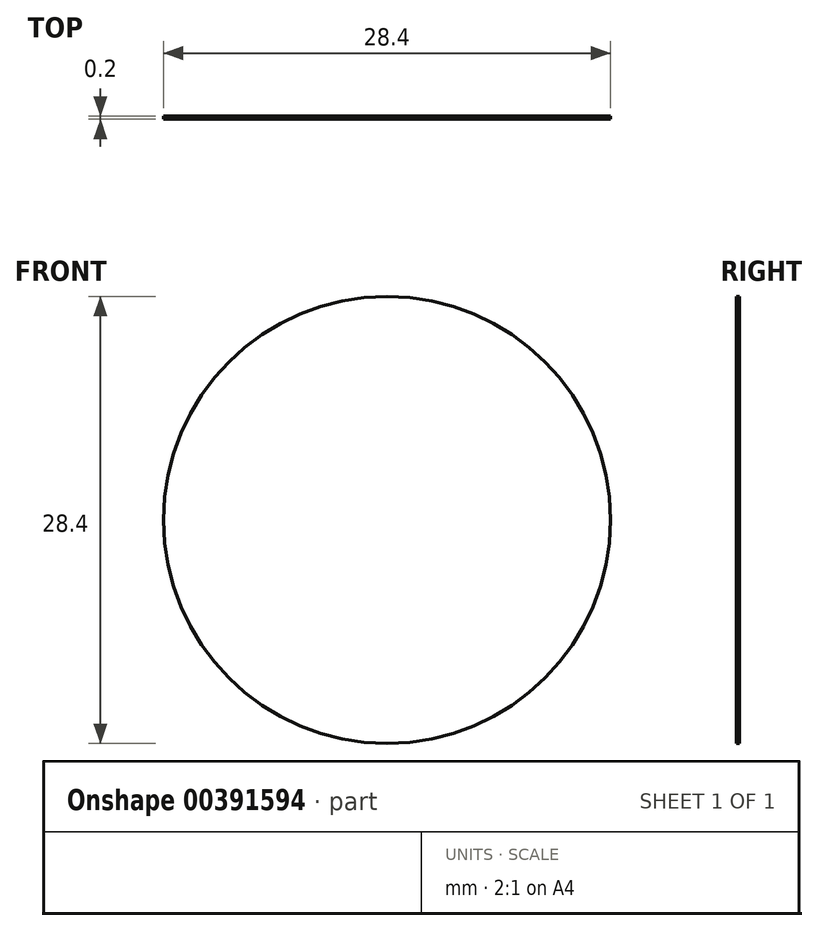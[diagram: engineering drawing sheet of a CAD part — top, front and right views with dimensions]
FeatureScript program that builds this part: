
annotation { "Feature Type Name" : "Feature", "Feature Type Description" : "" }
export const myFeature = defineFeature(function(context is Context, id is Id, definition is map)
    precondition{}
    {
        {
            var Q0;
            Q0=qCreatedBy(makeId("Front.planeOp"),FACE);
            var sketch = newSketch(context, id + "F0", { "sketchPlane" : qUnion([Q0])});
            skCircle(sketch, "E0", {"center": v(0, 0) * mm, "radius": 8 * mm, "construction": true});
            skCircle(sketch, "E1", {"center": v(0, 0) * mm, "radius": 10.5 * mm, "construction": true});
            skLineSegment(sketch, "E2", {"start": v(0, 8) * mm, "end": v(0.75, 8) * mm, "construction": true});
            skLineSegment(sketch, "E3", {"start": v(0.75, 8) * mm, "end": v(0.75, 13.5) * mm, "construction": true});
            skLineSegment(sketch, "E4", {"start": v(0.75, 13.5) * mm, "end": v(0, 13.5) * mm, "construction": true});
            skLineSegment(sketch, "E5", {"start": v(0, 13.5) * mm, "end": v(-0.75, 13.5) * mm, "construction": true});
            skLineSegment(sketch, "E6", {"start": v(-0.75, 13.5) * mm, "end": v(-0.75, 8) * mm, "construction": true});
            skLineSegment(sketch, "E7", {"start": v(-0.75, 8) * mm, "end": v(0, 8) * mm, "construction": true});
            skLineSegment(sketch, "E8.1.0", {"start": v(-3.35, 7.3) * mm, "end": v(-6.1, 12.07) * mm});
            skLineSegment(sketch, "E8.1.1", {"start": v(-7.4, 11.32) * mm, "end": v(-4.65, 6.55) * mm});
            skLineSegment(sketch, "E8.1.2", {"start": v(-4.65, 6.55) * mm, "end": v(-4, 6.93) * mm});
            skLineSegment(sketch, "E8.1.3", {"start": v(-4, 6.93) * mm, "end": v(-3.35, 7.3) * mm});
            skLineSegment(sketch, "E8.1.4", {"start": v(-6.1, 12.07) * mm, "end": v(-6.75, 11.7) * mm});
            skLineSegment(sketch, "E8.1.5", {"start": v(-6.75, 11.7) * mm, "end": v(-7.4, 11.32) * mm});
            skLineSegment(sketch, "E8.2.0", {"start": v(-6.55, 4.65) * mm, "end": v(-11.32, 7.4) * mm});
            skLineSegment(sketch, "E8.2.1", {"start": v(-12.07, 6.1) * mm, "end": v(-7.3, 3.35) * mm});
            skLineSegment(sketch, "E8.2.2", {"start": v(-7.3, 3.35) * mm, "end": v(-6.93, 4) * mm});
            skLineSegment(sketch, "E8.2.3", {"start": v(-6.93, 4) * mm, "end": v(-6.55, 4.65) * mm});
            skLineSegment(sketch, "E8.2.4", {"start": v(-11.32, 7.4) * mm, "end": v(-11.7, 6.75) * mm});
            skLineSegment(sketch, "E8.2.5", {"start": v(-11.7, 6.75) * mm, "end": v(-12.07, 6.1) * mm});
            skLineSegment(sketch, "E8.3.0", {"start": v(-8, 0.75) * mm, "end": v(-13.5, 0.75) * mm, "construction": true});
            skLineSegment(sketch, "E8.3.1", {"start": v(-13.5, -0.75) * mm, "end": v(-8, -0.75) * mm, "construction": true});
            skLineSegment(sketch, "E8.3.2", {"start": v(-8, -0.75) * mm, "end": v(-8, 0) * mm, "construction": true});
            skLineSegment(sketch, "E8.3.3", {"start": v(-8, 0) * mm, "end": v(-8, 0.75) * mm, "construction": true});
            skLineSegment(sketch, "E8.3.4", {"start": v(-13.5, 0.75) * mm, "end": v(-13.5, 0) * mm, "construction": true});
            skLineSegment(sketch, "E8.3.5", {"start": v(-13.5, 0) * mm, "end": v(-13.5, -0.75) * mm, "construction": true});
            skLineSegment(sketch, "E8.4.0", {"start": v(-7.3, -3.35) * mm, "end": v(-12.07, -6.1) * mm});
            skLineSegment(sketch, "E8.4.1", {"start": v(-11.32, -7.4) * mm, "end": v(-6.55, -4.65) * mm});
            skLineSegment(sketch, "E8.4.2", {"start": v(-6.55, -4.65) * mm, "end": v(-6.93, -4) * mm});
            skLineSegment(sketch, "E8.4.3", {"start": v(-6.93, -4) * mm, "end": v(-7.3, -3.35) * mm});
            skLineSegment(sketch, "E8.4.4", {"start": v(-12.07, -6.1) * mm, "end": v(-11.7, -6.75) * mm});
            skLineSegment(sketch, "E8.4.5", {"start": v(-11.7, -6.75) * mm, "end": v(-11.32, -7.4) * mm});
            skLineSegment(sketch, "E8.5.0", {"start": v(-4.65, -6.55) * mm, "end": v(-7.4, -11.32) * mm});
            skLineSegment(sketch, "E8.5.1", {"start": v(-6.1, -12.07) * mm, "end": v(-3.35, -7.3) * mm});
            skLineSegment(sketch, "E8.5.2", {"start": v(-3.35, -7.3) * mm, "end": v(-4, -6.93) * mm});
            skLineSegment(sketch, "E8.5.3", {"start": v(-4, -6.93) * mm, "end": v(-4.65, -6.55) * mm});
            skLineSegment(sketch, "E8.5.4", {"start": v(-7.4, -11.32) * mm, "end": v(-6.75, -11.7) * mm});
            skLineSegment(sketch, "E8.5.5", {"start": v(-6.75, -11.7) * mm, "end": v(-6.1, -12.07) * mm});
            skLineSegment(sketch, "E8.6.0", {"start": v(-0.75, -8) * mm, "end": v(-0.75, -13.5) * mm, "construction": true});
            skLineSegment(sketch, "E8.6.1", {"start": v(0.75, -13.5) * mm, "end": v(0.75, -8) * mm, "construction": true});
            skLineSegment(sketch, "E8.6.2", {"start": v(0.75, -8) * mm, "end": v(0, -8) * mm, "construction": true});
            skLineSegment(sketch, "E8.6.3", {"start": v(0, -8) * mm, "end": v(-0.75, -8) * mm, "construction": true});
            skLineSegment(sketch, "E8.6.4", {"start": v(-0.75, -13.5) * mm, "end": v(0, -13.5) * mm, "construction": true});
            skLineSegment(sketch, "E8.6.5", {"start": v(0, -13.5) * mm, "end": v(0.75, -13.5) * mm, "construction": true});
            skLineSegment(sketch, "E8.7.0", {"start": v(3.35, -7.3) * mm, "end": v(6.1, -12.07) * mm});
            skLineSegment(sketch, "E8.7.1", {"start": v(7.4, -11.32) * mm, "end": v(4.65, -6.55) * mm});
            skLineSegment(sketch, "E8.7.2", {"start": v(4.65, -6.55) * mm, "end": v(4, -6.93) * mm});
            skLineSegment(sketch, "E8.7.3", {"start": v(4, -6.93) * mm, "end": v(3.35, -7.3) * mm});
            skLineSegment(sketch, "E8.7.4", {"start": v(6.1, -12.07) * mm, "end": v(6.75, -11.7) * mm});
            skLineSegment(sketch, "E8.7.5", {"start": v(6.75, -11.7) * mm, "end": v(7.4, -11.32) * mm});
            skLineSegment(sketch, "E8.8.0", {"start": v(6.55, -4.65) * mm, "end": v(11.32, -7.4) * mm});
            skLineSegment(sketch, "E8.8.1", {"start": v(12.07, -6.1) * mm, "end": v(7.3, -3.35) * mm});
            skLineSegment(sketch, "E8.8.2", {"start": v(7.3, -3.35) * mm, "end": v(6.93, -4) * mm});
            skLineSegment(sketch, "E8.8.3", {"start": v(6.93, -4) * mm, "end": v(6.55, -4.65) * mm});
            skLineSegment(sketch, "E8.8.4", {"start": v(11.32, -7.4) * mm, "end": v(11.7, -6.75) * mm});
            skLineSegment(sketch, "E8.8.5", {"start": v(11.7, -6.75) * mm, "end": v(12.07, -6.1) * mm});
            skLineSegment(sketch, "E8.9.0", {"start": v(8, -0.75) * mm, "end": v(13.5, -0.75) * mm, "construction": true});
            skLineSegment(sketch, "E8.9.1", {"start": v(13.5, 0.75) * mm, "end": v(8, 0.75) * mm, "construction": true});
            skLineSegment(sketch, "E8.9.2", {"start": v(8, 0.75) * mm, "end": v(8, 0) * mm, "construction": true});
            skLineSegment(sketch, "E8.9.3", {"start": v(8, 0) * mm, "end": v(8, -0.75) * mm, "construction": true});
            skLineSegment(sketch, "E8.9.4", {"start": v(13.5, -0.75) * mm, "end": v(13.5, 0) * mm, "construction": true});
            skLineSegment(sketch, "E8.9.5", {"start": v(13.5, 0) * mm, "end": v(13.5, 0.75) * mm, "construction": true});
            skLineSegment(sketch, "E8.10.0", {"start": v(7.3, 3.35) * mm, "end": v(12.07, 6.1) * mm});
            skLineSegment(sketch, "E8.10.1", {"start": v(11.32, 7.4) * mm, "end": v(6.55, 4.65) * mm});
            skLineSegment(sketch, "E8.10.2", {"start": v(6.55, 4.65) * mm, "end": v(6.93, 4) * mm});
            skLineSegment(sketch, "E8.10.3", {"start": v(6.93, 4) * mm, "end": v(7.3, 3.35) * mm});
            skLineSegment(sketch, "E8.10.4", {"start": v(12.07, 6.1) * mm, "end": v(11.7, 6.75) * mm});
            skLineSegment(sketch, "E8.10.5", {"start": v(11.7, 6.75) * mm, "end": v(11.32, 7.4) * mm});
            skLineSegment(sketch, "E8.11.0", {"start": v(4.65, 6.55) * mm, "end": v(7.4, 11.32) * mm});
            skLineSegment(sketch, "E8.11.1", {"start": v(6.1, 12.07) * mm, "end": v(3.35, 7.3) * mm});
            skLineSegment(sketch, "E8.11.2", {"start": v(3.35, 7.3) * mm, "end": v(4, 6.93) * mm});
            skLineSegment(sketch, "E8.11.3", {"start": v(4, 6.93) * mm, "end": v(4.65, 6.55) * mm});
            skLineSegment(sketch, "E8.11.4", {"start": v(7.4, 11.32) * mm, "end": v(6.75, 11.7) * mm});
            skLineSegment(sketch, "E8.11.5", {"start": v(6.75, 11.7) * mm, "end": v(6.1, 12.07) * mm});
            skCircle(sketch, "E9", {"center": v(0, 0) * mm, "radius": 13.5 * mm, "construction": true});
            skSolve(sketch);
        }
        {
            var Q0;
            Q0=qCreatedBy(makeId("Front.planeOp"),FACE);
            var sketch = newSketch(context, id + "F1", { "sketchPlane" : qUnion([Q0])});
            skText(sketch, "E10", { "text": "12", "fontName": "AllertaStencil-Regular.ttf"});
            skText(sketch, "E11", { "text": "6", "fontName": "AllertaStencil-Regular.ttf"});
            skText(sketch, "E12", { "text": "9", "fontName": "AllertaStencil-Regular.ttf"});
            skPoint(sketch, "E13", {"position": v(-9.75, 0) * mm});
            skText(sketch, "E14", { "text": "3", "fontName": "AllertaStencil-Regular.ttf"});
            skCircle(sketch, "E15", {"center": v(0, 0) * mm, "radius": 9.75 * mm, "construction": true});
            skCircle(sketch, "E16", {"center": v(0, 0) * mm, "radius": 6 * mm, "construction": true});
            skLineSegment(sketch, "E17", {"start": v(0, 0) * mm, "end": v(0, 9.75) * mm, "construction": true});
            skLineSegment(sketch, "E18.1.0", {"start": v(0, 0) * mm, "end": v(-9.75, 0) * mm, "construction": true});
            skLineSegment(sketch, "E18.2.0", {"start": v(0, 0) * mm, "end": v(0, -9.75) * mm, "construction": true});
            skLineSegment(sketch, "E18.3.0", {"start": v(0, 0) * mm, "end": v(9.75, 0) * mm, "construction": true});
            skPoint(sketch, "E19", {"position": v(9.75, 0) * mm});
            const initialGuessF1  = {"E10": [-0.00263, 0.006, 1, 0, 0.00375], "E11": [-0.00164, -0.00975, 1, 0, 0.00375], "E12": [-0.00975, -0.00188, 1, 0, 0.00375], "E14": [0.00681, -0.00187, 1, 0, 0.00375]};
            skSetInitialGuess(sketch, initialGuessF1);
            skSolve(sketch);
        }
        {
            var Q0;
            Q0=qCreatedBy(makeId("Front.planeOp"),FACE);
            var sketch = newSketch(context, id + "F2", { "sketchPlane" : qUnion([Q0])});
            skLineSegment(sketch, "E20", {"start": v(0, 9.86) * mm, "end": v(2.1, 13.5) * mm});
            skLineSegment(sketch, "E21", {"start": v(2.1, 13.5) * mm, "end": v(-2.1, 13.5) * mm});
            skLineSegment(sketch, "E22", {"start": v(-2.1, 13.5) * mm, "end": v(0, 9.86) * mm});
            skLineSegment(sketch, "E23", {"start": v(-10.34, 0) * mm, "end": v(-10.34, 1.25) * mm});
            skLineSegment(sketch, "E24", {"start": v(-10.34, 1.25) * mm, "end": v(-13.44, 1.25) * mm});
            skLineSegment(sketch, "E25", {"start": v(-13.44, 1.25) * mm, "end": v(-13.44, -1.25) * mm});
            skLineSegment(sketch, "E26", {"start": v(-13.44, -1.25) * mm, "end": v(-10.34, -1.25) * mm});
            skLineSegment(sketch, "E27", {"start": v(-10.34, -1.25) * mm, "end": v(-10.34, 0) * mm});
            skCircle(sketch, "E28", {"center": v(0, 0) * mm, "radius": 11.25 * mm, "construction": true});
            skLineSegment(sketch, "E29.1.0", {"start": v(-1.25, -10.34) * mm, "end": v(-1.25, -13.44) * mm});
            skLineSegment(sketch, "E29.1.1", {"start": v(-1.25, -13.44) * mm, "end": v(1.25, -13.44) * mm});
            skLineSegment(sketch, "E29.1.2", {"start": v(1.25, -13.44) * mm, "end": v(1.25, -10.34) * mm});
            skLineSegment(sketch, "E29.1.3", {"start": v(1.25, -10.34) * mm, "end": v(0, -10.34) * mm});
            skLineSegment(sketch, "E29.1.4", {"start": v(0, -10.34) * mm, "end": v(-1.25, -10.34) * mm});
            skLineSegment(sketch, "E29.2.0", {"start": v(10.34, -1.25) * mm, "end": v(13.44, -1.25) * mm});
            skLineSegment(sketch, "E29.2.1", {"start": v(13.44, -1.25) * mm, "end": v(13.44, 1.25) * mm});
            skLineSegment(sketch, "E29.2.2", {"start": v(13.44, 1.25) * mm, "end": v(10.34, 1.25) * mm});
            skLineSegment(sketch, "E29.2.3", {"start": v(10.34, 1.25) * mm, "end": v(10.34, 0) * mm});
            skLineSegment(sketch, "E29.2.4", {"start": v(10.34, 0) * mm, "end": v(10.34, -1.25) * mm});
            skLineSegment(sketch, "E29.anchor1", {"start": v(0, 0) * mm, "end": v(-10.34, 0) * mm, "construction": true});
            skLineSegment(sketch, "E29.anchor2", {"start": v(0, 0) * mm, "end": v(10.34, 0) * mm, "construction": true});
            skCircle(sketch, "E30", {"center": v(0, 0) * mm, "radius": 14.2 * mm, "construction": true});
            skCircle(sketch, "E31", {"center": v(0, 0) * mm, "radius": 13.5 * mm, "construction": true});
            skLineSegment(sketch, "E32", {"start": v(0, 13.5) * mm, "end": v(0, 11.25) * mm, "construction": true});
            skCircle(sketch, "E33", {"center": v(0, 12.38) * mm, "radius": 1.13 * mm, "construction": true});
            skCircle(sketch, "E34.1.0", {"center": v(-6.19, 10.72) * mm, "radius": 1.13 * mm, "construction": true});
            skCircle(sketch, "E34.2.0", {"center": v(-10.72, 6.19) * mm, "radius": 1.13 * mm, "construction": true});
            skCircle(sketch, "E34.3.0", {"center": v(-12.38, 0) * mm, "radius": 1.13 * mm, "construction": true});
            skCircle(sketch, "E34.4.0", {"center": v(-10.72, -6.19) * mm, "radius": 1.13 * mm, "construction": true});
            skCircle(sketch, "E34.5.0", {"center": v(-6.19, -10.72) * mm, "radius": 1.13 * mm, "construction": true});
            skCircle(sketch, "E34.6.0", {"center": v(0, -12.38) * mm, "radius": 1.13 * mm, "construction": true});
            skCircle(sketch, "E34.7.0", {"center": v(6.19, -10.72) * mm, "radius": 1.13 * mm, "construction": true});
            skCircle(sketch, "E34.8.0", {"center": v(10.72, -6.19) * mm, "radius": 1.13 * mm, "construction": true});
            skCircle(sketch, "E34.9.0", {"center": v(12.38, 0) * mm, "radius": 1.13 * mm, "construction": true});
            skCircle(sketch, "E34.10.0", {"center": v(10.72, 6.19) * mm, "radius": 1.13 * mm, "construction": true});
            skCircle(sketch, "E34.11.0", {"center": v(6.19, 10.72) * mm, "radius": 1.13 * mm, "construction": true});
            skSolve(sketch);
        }
        {
            var Q0;
            Q0=qCreatedBy(makeId("Front.planeOp"),FACE);
            var sketch = newSketch(context, id + "F3", { "sketchPlane" : qUnion([Q0])});
            skCircle(sketch, "E35", {"center": v(0, 0) * mm, "radius": 14.2 * mm});
            skSolve(sketch);
        }
        {
            var Q0;
            Q0=qCreatedBy(makeId("Front.planeOp"),FACE);
            var sketch = newSketch(context, id + "F4", { "sketchPlane" : qUnion([Q0])});
            skArc(sketch, "E36", {"start": v(-2.79, 5.35) * mm, "mid": v(-2.89, 5.26) * mm, "end": v(-2.8, 5.15) * mm});
            skCircle(sketch, "E37", {"center": v(-1.36, 4.5) * mm, "radius": 0.5 * mm});
            skCircle(sketch, "E38", {"center": v(-1.36, 4.5) * mm, "radius": 0.3 * mm});
            skArc(sketch, "E39", {"start": v(0.2, 4.78) * mm, "mid": v(-0.7, 4.6) * mm, "end": v(0.06, 4.08) * mm});
            skArc(sketch, "E40", {"start": v(0.04, 4.67) * mm, "mid": v(-0.5, 4.56) * mm, "end": v(-0.05, 4.25) * mm});
            skCircle(sketch, "E41", {"center": v(1.59, 4.5) * mm, "radius": 0.5 * mm});
            skCircle(sketch, "E42", {"center": v(1.59, 4.5) * mm, "radius": 0.3 * mm});
            skLineSegment(sketch, "E43", {"start": v(-1.36, 4.5) * mm, "end": v(-0.21, 4.5) * mm, "construction": true});
            skLineSegment(sketch, "E44", {"start": v(0.69, 4.5) * mm, "end": v(1.59, 4.5) * mm, "construction": true});
            skLineSegment(sketch, "E45", {"start": v(0.69, 4.5) * mm, "end": v(-0.21, 4.5) * mm, "construction": true});
            skLineSegment(sketch, "E46", {"start": v(-0.21, 5) * mm, "end": v(-1.36, 5) * mm, "construction": true});
            skLineSegment(sketch, "E47", {"start": v(-1.36, 4) * mm, "end": v(-0.21, 4) * mm, "construction": true});
            skLineSegment(sketch, "E48", {"start": v(-0.21, 4) * mm, "end": v(1.59, 4) * mm, "construction": true});
            skArc(sketch, "E49", {"start": v(0.39, 5) * mm, "mid": v(0.29, 4.9) * mm, "end": v(0.39, 4.8) * mm});
            skArc(sketch, "E50", {"start": v(0.99, 4.8) * mm, "mid": v(1.09, 4.9) * mm, "end": v(0.99, 5) * mm});
            skArc(sketch, "E51", {"start": v(0.45, 4.12) * mm, "mid": v(0.53, 4) * mm, "end": v(0.65, 4.08) * mm});
            skCircle(sketch, "E52", {"center": v(2.29, 4.1) * mm, "radius": 0.1 * mm});
            skCircle(sketch, "E53", {"center": v(3.08, 4.91) * mm, "radius": 0.1 * mm});
            skCircle(sketch, "E54", {"center": v(2.99, 4.1) * mm, "radius": 0.1 * mm});
            skArc(sketch, "E55", {"start": v(0.04, 4.67) * mm, "mid": v(0.17, 4.64) * mm, "end": v(0.2, 4.78) * mm});
            skArc(sketch, "E56", {"start": v(0.06, 4.08) * mm, "mid": v(0.1, 4.22) * mm, "end": v(-0.05, 4.25) * mm});
            skArc(sketch, "E57", {"start": v(-3, 4.12) * mm, "mid": v(-2.99, 4.04) * mm, "end": v(-2.91, 4) * mm});
            skArc(sketch, "E58", {"start": v(-2.41, 4.2) * mm, "mid": v(-2.19, 4.42) * mm, "end": v(-2.41, 4.65) * mm});
            skArc(sketch, "E59", {"start": v(-2.41, 4.85) * mm, "mid": v(-2.26, 5) * mm, "end": v(-2.41, 5.15) * mm});
            skArc(sketch, "E60", {"start": v(-2.15, 4.76) * mm, "mid": v(-2.1, 5.14) * mm, "end": v(-2.41, 5.35) * mm});
            skLineSegment(sketch, "E61", {"start": v(-1.36, 4) * mm, "end": v(-2.91, 4) * mm, "construction": true});
            skLineSegment(sketch, "E62", {"start": v(-2.91, 4) * mm, "end": v(-2.41, 4) * mm});
            skLineSegment(sketch, "E63", {"start": v(-2.8, 5.15) * mm, "end": v(-3, 4.12) * mm});
            skLineSegment(sketch, "E64", {"start": v(-2.79, 5.35) * mm, "end": v(-2.41, 5.35) * mm});
            skLineSegment(sketch, "E65", {"start": v(-1.82, 5.35) * mm, "end": v(2.51, 5.35) * mm});
            skLineSegment(sketch, "E66", {"start": v(2.61, 5.23) * mm, "end": v(2.45, 4.41) * mm});
            skLineSegment(sketch, "E67", {"start": v(2.45, 4.41) * mm, "end": v(3, 4.98) * mm});
            skLineSegment(sketch, "E68", {"start": v(3.15, 4.84) * mm, "end": v(2.86, 4.55) * mm});
            skLineSegment(sketch, "E69", {"start": v(2.86, 4.55) * mm, "end": v(3.08, 4.15) * mm});
            skLineSegment(sketch, "E70", {"start": v(2.9, 4.05) * mm, "end": v(2.71, 4.4) * mm});
            skLineSegment(sketch, "E71", {"start": v(2.71, 4.4) * mm, "end": v(2.36, 4.03) * mm});
            skLineSegment(sketch, "E72", {"start": v(2.2, 4.12) * mm, "end": v(2.4, 5.15) * mm});
            skLineSegment(sketch, "E73", {"start": v(2.4, 5.15) * mm, "end": v(-1.82, 5.15) * mm});
            skArc(sketch, "E74", {"start": v(-1.82, 5.35) * mm, "mid": v(-1.92, 5.25) * mm, "end": v(-1.82, 5.15) * mm});
            skLineSegment(sketch, "E75", {"start": v(0.39, 5) * mm, "end": v(0.99, 5) * mm});
            skLineSegment(sketch, "E76", {"start": v(0.39, 4.8) * mm, "end": v(0.59, 4.8) * mm});
            skLineSegment(sketch, "E77", {"start": v(0.59, 4.8) * mm, "end": v(0.45, 4.12) * mm});
            skLineSegment(sketch, "E78", {"start": v(0.65, 4.08) * mm, "end": v(0.8, 4.8) * mm});
            skLineSegment(sketch, "E79", {"start": v(0.8, 4.8) * mm, "end": v(0.99, 4.8) * mm});
            skLineSegment(sketch, "E80", {"start": v(1.59, 4) * mm, "end": v(2.29, 4) * mm, "construction": true});
            skLineSegment(sketch, "E81", {"start": v(2.29, 4) * mm, "end": v(2.99, 4) * mm, "construction": true});
            skLineSegment(sketch, "E82", {"start": v(2.29, 4.1) * mm, "end": v(3.08, 4.91) * mm, "construction": true});
            skArc(sketch, "E83", {"start": v(2.61, 5.23) * mm, "mid": v(2.59, 5.31) * mm, "end": v(2.51, 5.35) * mm});
            skLineSegment(sketch, "E84", {"start": v(0.99, 5) * mm, "end": v(1.84, 5) * mm, "construction": true});
            skLineSegment(sketch, "E85", {"start": v(0, 4.17) * mm, "end": v(0.12, 4.73) * mm, "construction": true});
            skLineSegment(sketch, "E86", {"start": v(0.59, 4.8) * mm, "end": v(0.8, 4.8) * mm, "construction": true});
            skLineSegment(sketch, "E87", {"start": v(0.39, 4.9) * mm, "end": v(0.99, 4.9) * mm, "construction": true});
            skPoint(sketch, "E88", {"position": v(0.69, 4.9) * mm});
            skPoint(sketch, "E89", {"position": v(0.69, 4.8) * mm});
            skLineSegment(sketch, "E90", {"start": v(-2.8, 4.2) * mm, "end": v(-2.7, 4.65) * mm});
            skLineSegment(sketch, "E91", {"start": v(-2.6, 5.15) * mm, "end": v(-2.41, 5.15) * mm});
            skLineSegment(sketch, "E92", {"start": v(-2.66, 4.85) * mm, "end": v(-2.41, 4.85) * mm});
            skLineSegment(sketch, "E93", {"start": v(-2.41, 4.65) * mm, "end": v(-2.7, 4.65) * mm});
            skLineSegment(sketch, "E94", {"start": v(-2.8, 4.2) * mm, "end": v(-2.41, 4.2) * mm});
            skLineSegment(sketch, "E95.trimOffspring", {"start": v(-2.66, 4.85) * mm, "end": v(-2.6, 5.15) * mm});
            skArc(sketch, "E96.trimOffspring", {"start": v(-2.41, 4) * mm, "mid": v(-2, 4.29) * mm, "end": v(-2.15, 4.76) * mm});
            skLineSegment(sketch, "E97", {"start": v(-2.99, 3.7) * mm, "end": v(2.99, 3.7) * mm, "construction": true});
            skPoint(sketch, "E97.startSnap0", {"position": v(-2.99, 4.04) * mm});
            skPoint(sketch, "E98", {"position": v(0, 3.7) * mm});
            skSolve(sketch);
        }
        {
            var Q0;
            Q0=qCreatedBy(makeId("Front.planeOp"),FACE);
            var sketch = newSketch(context, id + "F5", { "sketchPlane" : qUnion([Q0])});
            skCircle(sketch, "E99", {"center": v(0, 0) * mm, "radius": 13.5 * mm, "construction": true});
            skCircle(sketch, "E100", {"center": v(0, 0) * mm, "radius": 12.25 * mm, "construction": true});
            skLineSegment(sketch, "E101", {"start": v(0.5, 13.5) * mm, "end": v(-0.5, 13.5) * mm, "construction": true});
            skLineSegment(sketch, "E102", {"start": v(-0.5, 13.5) * mm, "end": v(-0.45, 12.24) * mm, "construction": true});
            skLineSegment(sketch, "E103", {"start": v(0.5, 13.5) * mm, "end": v(0.45, 12.24) * mm, "construction": true});
            skLineSegment(sketch, "E104", {"start": v(0, 12.25) * mm, "end": v(0.45, 12.25) * mm, "construction": true});
            skLineSegment(sketch, "E105", {"start": v(0, 12.25) * mm, "end": v(-0.45, 12.25) * mm, "construction": true});
            skLineSegment(sketch, "E106.1.0", {"start": v(-0.91, 13.48) * mm, "end": v(-0.83, 12.22) * mm, "construction": true});
            skLineSegment(sketch, "E106.1.1", {"start": v(-1.9, 13.37) * mm, "end": v(-1.73, 12.13) * mm, "construction": true});
            skLineSegment(sketch, "E106.1.2", {"start": v(-0.91, 13.48) * mm, "end": v(-1.9, 13.37) * mm, "construction": true});
            skLineSegment(sketch, "E106.1.3", {"start": v(-1.28, 12.18) * mm, "end": v(-1.73, 12.14) * mm, "construction": true});
            skLineSegment(sketch, "E106.1.4", {"start": v(-1.28, 12.18) * mm, "end": v(-0.83, 12.23) * mm, "construction": true});
            skLineSegment(sketch, "E106.2.0", {"start": v(-2.32, 13.3) * mm, "end": v(-2.1, 12.07) * mm});
            skLineSegment(sketch, "E106.2.1", {"start": v(-3.3, 13.1) * mm, "end": v(-2.99, 11.88) * mm});
            skLineSegment(sketch, "E106.2.2", {"start": v(-2.32, 13.3) * mm, "end": v(-3.3, 13.1) * mm});
            skLineSegment(sketch, "E106.2.3", {"start": v(-2.55, 11.98) * mm, "end": v(-3, 11.89) * mm});
            skLineSegment(sketch, "E106.2.4", {"start": v(-2.55, 11.98) * mm, "end": v(-2.1, 12.08) * mm});
            skLineSegment(sketch, "E107.2.3.0", {"start": v(-3.7, 13) * mm, "end": v(-3.35, 11.78) * mm});
            skLineSegment(sketch, "E107.3.3.0", {"start": v(-4.65, 12.68) * mm, "end": v(-4.21, 11.5) * mm});
            skLineSegment(sketch, "E107.6.3.0", {"start": v(-3.7, 13) * mm, "end": v(-4.65, 12.68) * mm});
            skLineSegment(sketch, "E107.9.3.0", {"start": v(-3.79, 11.65) * mm, "end": v(-4.22, 11.51) * mm});
            skLineSegment(sketch, "E107.12.3.0", {"start": v(-3.79, 11.65) * mm, "end": v(-3.35, 11.8) * mm});
            skLineSegment(sketch, "E107.2.4.0", {"start": v(-5.03, 12.54) * mm, "end": v(-4.56, 11.37) * mm});
            skLineSegment(sketch, "E107.3.4.0", {"start": v(-5.95, 12.13) * mm, "end": v(-5.4, 11) * mm});
            skLineSegment(sketch, "E107.6.4.0", {"start": v(-5.03, 12.54) * mm, "end": v(-5.95, 12.13) * mm});
            skLineSegment(sketch, "E107.9.4.0", {"start": v(-4.98, 11.2) * mm, "end": v(-5.4, 11) * mm});
            skLineSegment(sketch, "E107.12.4.0", {"start": v(-4.98, 11.2) * mm, "end": v(-4.57, 11.38) * mm});
            skLineSegment(sketch, "E107.2.5.0", {"start": v(-6.32, 11.94) * mm, "end": v(-5.73, 10.83) * mm});
            skLineSegment(sketch, "E107.3.5.0", {"start": v(-7.18, 11.44) * mm, "end": v(-6.51, 10.37) * mm});
            skLineSegment(sketch, "E107.6.5.0", {"start": v(-6.32, 11.94) * mm, "end": v(-7.18, 11.44) * mm});
            skLineSegment(sketch, "E107.9.5.0", {"start": v(-6.12, 10.6) * mm, "end": v(-6.52, 10.38) * mm});
            skLineSegment(sketch, "E107.12.5.0", {"start": v(-6.12, 10.6) * mm, "end": v(-5.73, 10.84) * mm});
            skLineSegment(sketch, "E107.2.6.0", {"start": v(-7.53, 11.22) * mm, "end": v(-6.83, 10.17) * mm});
            skLineSegment(sketch, "E107.3.6.0", {"start": v(-8.34, 10.63) * mm, "end": v(-7.56, 9.64) * mm});
            skLineSegment(sketch, "E107.6.6.0", {"start": v(-7.53, 11.22) * mm, "end": v(-8.34, 10.63) * mm});
            skLineSegment(sketch, "E107.9.6.0", {"start": v(-7.2, 9.91) * mm, "end": v(-7.57, 9.64) * mm});
            skLineSegment(sketch, "E107.12.6.0", {"start": v(-7.2, 9.91) * mm, "end": v(-6.83, 10.18) * mm});
            skLineSegment(sketch, "E107.2.7.0", {"start": v(-8.66, 10.37) * mm, "end": v(-7.85, 9.4) * mm});
            skLineSegment(sketch, "E107.3.7.0", {"start": v(-9.4, 9.7) * mm, "end": v(-8.53, 8.8) * mm});
            skLineSegment(sketch, "E107.6.7.0", {"start": v(-8.66, 10.37) * mm, "end": v(-9.4, 9.7) * mm});
            skLineSegment(sketch, "E107.9.7.0", {"start": v(-8.2, 9.1) * mm, "end": v(-8.53, 8.8) * mm});
            skLineSegment(sketch, "E107.12.7.0", {"start": v(-8.2, 9.1) * mm, "end": v(-7.86, 9.4) * mm});
            skLineSegment(sketch, "E107.2.8.0", {"start": v(-9.7, 9.4) * mm, "end": v(-8.8, 8.53) * mm});
            skLineSegment(sketch, "E107.3.8.0", {"start": v(-10.37, 8.66) * mm, "end": v(-9.4, 7.85) * mm});
            skLineSegment(sketch, "E107.6.8.0", {"start": v(-9.7, 9.4) * mm, "end": v(-10.37, 8.66) * mm});
            skLineSegment(sketch, "E107.9.8.0", {"start": v(-9.1, 8.2) * mm, "end": v(-9.4, 7.86) * mm});
            skLineSegment(sketch, "E107.12.8.0", {"start": v(-9.1, 8.2) * mm, "end": v(-8.8, 8.53) * mm});
            skLineSegment(sketch, "E107.2.9.0", {"start": v(-10.63, 8.34) * mm, "end": v(-9.64, 7.56) * mm});
            skLineSegment(sketch, "E107.3.9.0", {"start": v(-11.22, 7.53) * mm, "end": v(-10.17, 6.83) * mm});
            skLineSegment(sketch, "E107.6.9.0", {"start": v(-10.63, 8.34) * mm, "end": v(-11.22, 7.53) * mm});
            skLineSegment(sketch, "E107.9.9.0", {"start": v(-9.91, 7.2) * mm, "end": v(-10.18, 6.83) * mm});
            skLineSegment(sketch, "E107.12.9.0", {"start": v(-9.91, 7.2) * mm, "end": v(-9.64, 7.57) * mm});
            skLineSegment(sketch, "E107.2.10.0", {"start": v(-11.44, 7.18) * mm, "end": v(-10.37, 6.51) * mm});
            skLineSegment(sketch, "E107.3.10.0", {"start": v(-11.94, 6.32) * mm, "end": v(-10.83, 5.73) * mm});
            skLineSegment(sketch, "E107.6.10.0", {"start": v(-11.44, 7.18) * mm, "end": v(-11.94, 6.32) * mm});
            skLineSegment(sketch, "E107.9.10.0", {"start": v(-10.6, 6.13) * mm, "end": v(-10.84, 5.73) * mm});
            skLineSegment(sketch, "E107.12.10.0", {"start": v(-10.6, 6.13) * mm, "end": v(-10.38, 6.52) * mm});
            skLineSegment(sketch, "E107.2.11.0", {"start": v(-12.13, 5.95) * mm, "end": v(-11, 5.4) * mm});
            skLineSegment(sketch, "E107.3.11.0", {"start": v(-12.54, 5.03) * mm, "end": v(-11.37, 4.56) * mm});
            skLineSegment(sketch, "E107.6.11.0", {"start": v(-12.13, 5.95) * mm, "end": v(-12.54, 5.03) * mm});
            skLineSegment(sketch, "E107.9.11.0", {"start": v(-11.2, 4.98) * mm, "end": v(-11.38, 4.57) * mm});
            skLineSegment(sketch, "E107.12.11.0", {"start": v(-11.2, 4.98) * mm, "end": v(-11, 5.4) * mm});
            skLineSegment(sketch, "E107.2.12.0", {"start": v(-12.68, 4.65) * mm, "end": v(-11.5, 4.21) * mm});
            skLineSegment(sketch, "E107.3.12.0", {"start": v(-13, 3.7) * mm, "end": v(-11.78, 3.35) * mm});
            skLineSegment(sketch, "E107.6.12.0", {"start": v(-12.68, 4.65) * mm, "end": v(-13, 3.7) * mm});
            skLineSegment(sketch, "E107.9.12.0", {"start": v(-11.65, 3.79) * mm, "end": v(-11.8, 3.35) * mm});
            skLineSegment(sketch, "E107.12.12.0", {"start": v(-11.65, 3.79) * mm, "end": v(-11.51, 4.22) * mm});
            skLineSegment(sketch, "E107.2.13.0", {"start": v(-13.1, 3.3) * mm, "end": v(-11.88, 2.99) * mm});
            skLineSegment(sketch, "E107.3.13.0", {"start": v(-13.3, 2.32) * mm, "end": v(-12.07, 2.1) * mm});
            skLineSegment(sketch, "E107.6.13.0", {"start": v(-13.1, 3.3) * mm, "end": v(-13.3, 2.32) * mm});
            skLineSegment(sketch, "E107.9.13.0", {"start": v(-11.98, 2.55) * mm, "end": v(-12.08, 2.1) * mm});
            skLineSegment(sketch, "E107.12.13.0", {"start": v(-11.98, 2.55) * mm, "end": v(-11.89, 3) * mm});
            skLineSegment(sketch, "E107.2.14.0", {"start": v(-13.37, 1.9) * mm, "end": v(-12.13, 1.73) * mm, "construction": true});
            skLineSegment(sketch, "E107.3.14.0", {"start": v(-13.48, 0.91) * mm, "end": v(-12.22, 0.83) * mm, "construction": true});
            skLineSegment(sketch, "E107.6.14.0", {"start": v(-13.37, 1.9) * mm, "end": v(-13.48, 0.91) * mm, "construction": true});
            skLineSegment(sketch, "E107.9.14.0", {"start": v(-12.18, 1.28) * mm, "end": v(-12.23, 0.83) * mm, "construction": true});
            skLineSegment(sketch, "E107.12.14.0", {"start": v(-12.18, 1.28) * mm, "end": v(-12.14, 1.73) * mm, "construction": true});
            skLineSegment(sketch, "E107.2.15.0", {"start": v(-13.5, 0.5) * mm, "end": v(-12.24, 0.45) * mm, "construction": true});
            skLineSegment(sketch, "E107.3.15.0", {"start": v(-13.5, -0.5) * mm, "end": v(-12.24, -0.45) * mm, "construction": true});
            skLineSegment(sketch, "E107.6.15.0", {"start": v(-13.5, 0.5) * mm, "end": v(-13.5, -0.5) * mm, "construction": true});
            skLineSegment(sketch, "E107.9.15.0", {"start": v(-12.25, 0) * mm, "end": v(-12.25, -0.45) * mm, "construction": true});
            skLineSegment(sketch, "E107.12.15.0", {"start": v(-12.25, 0) * mm, "end": v(-12.25, 0.45) * mm, "construction": true});
            skLineSegment(sketch, "E107.2.16.0", {"start": v(-13.48, -0.91) * mm, "end": v(-12.22, -0.83) * mm, "construction": true});
            skLineSegment(sketch, "E107.3.16.0", {"start": v(-13.37, -1.9) * mm, "end": v(-12.13, -1.73) * mm, "construction": true});
            skLineSegment(sketch, "E107.6.16.0", {"start": v(-13.48, -0.91) * mm, "end": v(-13.37, -1.9) * mm, "construction": true});
            skLineSegment(sketch, "E107.9.16.0", {"start": v(-12.18, -1.28) * mm, "end": v(-12.14, -1.73) * mm, "construction": true});
            skLineSegment(sketch, "E107.12.16.0", {"start": v(-12.18, -1.28) * mm, "end": v(-12.23, -0.83) * mm, "construction": true});
            skLineSegment(sketch, "E107.2.17.0", {"start": v(-13.3, -2.32) * mm, "end": v(-12.07, -2.1) * mm});
            skLineSegment(sketch, "E107.3.17.0", {"start": v(-13.1, -3.3) * mm, "end": v(-11.88, -2.99) * mm});
            skLineSegment(sketch, "E107.6.17.0", {"start": v(-13.3, -2.32) * mm, "end": v(-13.1, -3.3) * mm});
            skLineSegment(sketch, "E107.9.17.0", {"start": v(-11.98, -2.55) * mm, "end": v(-11.89, -3) * mm});
            skLineSegment(sketch, "E107.12.17.0", {"start": v(-11.98, -2.55) * mm, "end": v(-12.08, -2.1) * mm});
            skLineSegment(sketch, "E107.2.18.0", {"start": v(-13, -3.7) * mm, "end": v(-11.78, -3.35) * mm});
            skLineSegment(sketch, "E107.3.18.0", {"start": v(-12.68, -4.65) * mm, "end": v(-11.5, -4.21) * mm});
            skLineSegment(sketch, "E107.6.18.0", {"start": v(-13, -3.7) * mm, "end": v(-12.68, -4.65) * mm});
            skLineSegment(sketch, "E107.9.18.0", {"start": v(-11.65, -3.79) * mm, "end": v(-11.51, -4.22) * mm});
            skLineSegment(sketch, "E107.12.18.0", {"start": v(-11.65, -3.79) * mm, "end": v(-11.8, -3.35) * mm});
            skLineSegment(sketch, "E107.2.19.0", {"start": v(-12.54, -5.03) * mm, "end": v(-11.37, -4.56) * mm});
            skLineSegment(sketch, "E107.3.19.0", {"start": v(-12.13, -5.95) * mm, "end": v(-11, -5.4) * mm});
            skLineSegment(sketch, "E107.6.19.0", {"start": v(-12.54, -5.03) * mm, "end": v(-12.13, -5.95) * mm});
            skLineSegment(sketch, "E107.9.19.0", {"start": v(-11.2, -4.98) * mm, "end": v(-11, -5.4) * mm});
            skLineSegment(sketch, "E107.12.19.0", {"start": v(-11.2, -4.98) * mm, "end": v(-11.38, -4.57) * mm});
            skLineSegment(sketch, "E107.2.20.0", {"start": v(-11.94, -6.32) * mm, "end": v(-10.83, -5.73) * mm});
            skLineSegment(sketch, "E107.3.20.0", {"start": v(-11.44, -7.18) * mm, "end": v(-10.37, -6.51) * mm});
            skLineSegment(sketch, "E107.6.20.0", {"start": v(-11.94, -6.32) * mm, "end": v(-11.44, -7.18) * mm});
            skLineSegment(sketch, "E107.9.20.0", {"start": v(-10.6, -6.12) * mm, "end": v(-10.38, -6.52) * mm});
            skLineSegment(sketch, "E107.12.20.0", {"start": v(-10.6, -6.12) * mm, "end": v(-10.84, -5.73) * mm});
            skLineSegment(sketch, "E107.2.21.0", {"start": v(-11.22, -7.53) * mm, "end": v(-10.17, -6.83) * mm});
            skLineSegment(sketch, "E107.3.21.0", {"start": v(-10.63, -8.34) * mm, "end": v(-9.64, -7.56) * mm});
            skLineSegment(sketch, "E107.6.21.0", {"start": v(-11.22, -7.53) * mm, "end": v(-10.63, -8.34) * mm});
            skLineSegment(sketch, "E107.9.21.0", {"start": v(-9.91, -7.2) * mm, "end": v(-9.64, -7.57) * mm});
            skLineSegment(sketch, "E107.12.21.0", {"start": v(-9.91, -7.2) * mm, "end": v(-10.18, -6.83) * mm});
            skLineSegment(sketch, "E107.2.22.0", {"start": v(-10.37, -8.66) * mm, "end": v(-9.4, -7.85) * mm});
            skLineSegment(sketch, "E107.3.22.0", {"start": v(-9.7, -9.4) * mm, "end": v(-8.8, -8.53) * mm});
            skLineSegment(sketch, "E107.6.22.0", {"start": v(-10.37, -8.66) * mm, "end": v(-9.7, -9.4) * mm});
            skLineSegment(sketch, "E107.9.22.0", {"start": v(-9.1, -8.2) * mm, "end": v(-8.8, -8.53) * mm});
            skLineSegment(sketch, "E107.12.22.0", {"start": v(-9.1, -8.2) * mm, "end": v(-9.4, -7.86) * mm});
            skLineSegment(sketch, "E107.2.23.0", {"start": v(-9.4, -9.7) * mm, "end": v(-8.53, -8.8) * mm});
            skLineSegment(sketch, "E107.3.23.0", {"start": v(-8.66, -10.37) * mm, "end": v(-7.85, -9.4) * mm});
            skLineSegment(sketch, "E107.6.23.0", {"start": v(-9.4, -9.7) * mm, "end": v(-8.66, -10.37) * mm});
            skLineSegment(sketch, "E107.9.23.0", {"start": v(-8.2, -9.1) * mm, "end": v(-7.86, -9.4) * mm});
            skLineSegment(sketch, "E107.12.23.0", {"start": v(-8.2, -9.1) * mm, "end": v(-8.53, -8.8) * mm});
            skLineSegment(sketch, "E107.2.24.0", {"start": v(-8.34, -10.63) * mm, "end": v(-7.56, -9.64) * mm});
            skLineSegment(sketch, "E107.3.24.0", {"start": v(-7.53, -11.22) * mm, "end": v(-6.83, -10.17) * mm});
            skLineSegment(sketch, "E107.6.24.0", {"start": v(-8.34, -10.63) * mm, "end": v(-7.53, -11.22) * mm});
            skLineSegment(sketch, "E107.9.24.0", {"start": v(-7.2, -9.91) * mm, "end": v(-6.83, -10.18) * mm});
            skLineSegment(sketch, "E107.12.24.0", {"start": v(-7.2, -9.91) * mm, "end": v(-7.57, -9.64) * mm});
            skLineSegment(sketch, "E107.2.25.0", {"start": v(-7.18, -11.44) * mm, "end": v(-6.51, -10.37) * mm});
            skLineSegment(sketch, "E107.3.25.0", {"start": v(-6.32, -11.94) * mm, "end": v(-5.73, -10.83) * mm});
            skLineSegment(sketch, "E107.6.25.0", {"start": v(-7.18, -11.44) * mm, "end": v(-6.32, -11.94) * mm});
            skLineSegment(sketch, "E107.9.25.0", {"start": v(-6.12, -10.6) * mm, "end": v(-5.73, -10.84) * mm});
            skLineSegment(sketch, "E107.12.25.0", {"start": v(-6.12, -10.6) * mm, "end": v(-6.52, -10.38) * mm});
            skLineSegment(sketch, "E107.2.26.0", {"start": v(-5.95, -12.13) * mm, "end": v(-5.4, -11) * mm});
            skLineSegment(sketch, "E107.3.26.0", {"start": v(-5.03, -12.54) * mm, "end": v(-4.56, -11.37) * mm});
            skLineSegment(sketch, "E107.6.26.0", {"start": v(-5.95, -12.13) * mm, "end": v(-5.03, -12.54) * mm});
            skLineSegment(sketch, "E107.9.26.0", {"start": v(-4.98, -11.2) * mm, "end": v(-4.57, -11.38) * mm});
            skLineSegment(sketch, "E107.12.26.0", {"start": v(-4.98, -11.2) * mm, "end": v(-5.4, -11) * mm});
            skLineSegment(sketch, "E107.2.27.0", {"start": v(-4.65, -12.68) * mm, "end": v(-4.21, -11.5) * mm});
            skLineSegment(sketch, "E107.3.27.0", {"start": v(-3.7, -13) * mm, "end": v(-3.35, -11.78) * mm});
            skLineSegment(sketch, "E107.6.27.0", {"start": v(-4.65, -12.68) * mm, "end": v(-3.7, -13) * mm});
            skLineSegment(sketch, "E107.9.27.0", {"start": v(-3.79, -11.65) * mm, "end": v(-3.35, -11.8) * mm});
            skLineSegment(sketch, "E107.12.27.0", {"start": v(-3.79, -11.65) * mm, "end": v(-4.22, -11.51) * mm});
            skLineSegment(sketch, "E107.2.28.0", {"start": v(-3.3, -13.1) * mm, "end": v(-2.99, -11.88) * mm});
            skLineSegment(sketch, "E107.3.28.0", {"start": v(-2.32, -13.3) * mm, "end": v(-2.1, -12.07) * mm});
            skLineSegment(sketch, "E107.6.28.0", {"start": v(-3.3, -13.1) * mm, "end": v(-2.32, -13.3) * mm});
            skLineSegment(sketch, "E107.9.28.0", {"start": v(-2.55, -11.98) * mm, "end": v(-2.1, -12.08) * mm});
            skLineSegment(sketch, "E107.12.28.0", {"start": v(-2.55, -11.98) * mm, "end": v(-3, -11.89) * mm});
            skLineSegment(sketch, "E107.2.29.0", {"start": v(-1.9, -13.37) * mm, "end": v(-1.73, -12.13) * mm, "construction": true});
            skLineSegment(sketch, "E107.3.29.0", {"start": v(-0.91, -13.48) * mm, "end": v(-0.83, -12.22) * mm, "construction": true});
            skLineSegment(sketch, "E107.6.29.0", {"start": v(-1.9, -13.37) * mm, "end": v(-0.91, -13.48) * mm, "construction": true});
            skLineSegment(sketch, "E107.9.29.0", {"start": v(-1.28, -12.18) * mm, "end": v(-0.83, -12.23) * mm, "construction": true});
            skLineSegment(sketch, "E107.12.29.0", {"start": v(-1.28, -12.18) * mm, "end": v(-1.73, -12.14) * mm, "construction": true});
            skLineSegment(sketch, "E107.2.30.0", {"start": v(-0.5, -13.5) * mm, "end": v(-0.45, -12.24) * mm, "construction": true});
            skLineSegment(sketch, "E107.3.30.0", {"start": v(0.5, -13.5) * mm, "end": v(0.45, -12.24) * mm, "construction": true});
            skLineSegment(sketch, "E107.6.30.0", {"start": v(-0.5, -13.5) * mm, "end": v(0.5, -13.5) * mm, "construction": true});
            skLineSegment(sketch, "E107.9.30.0", {"start": v(0, -12.25) * mm, "end": v(0.45, -12.25) * mm, "construction": true});
            skLineSegment(sketch, "E107.12.30.0", {"start": v(0, -12.25) * mm, "end": v(-0.45, -12.25) * mm, "construction": true});
            skLineSegment(sketch, "E107.2.31.0", {"start": v(0.91, -13.48) * mm, "end": v(0.83, -12.22) * mm, "construction": true});
            skLineSegment(sketch, "E107.3.31.0", {"start": v(1.9, -13.37) * mm, "end": v(1.73, -12.13) * mm, "construction": true});
            skLineSegment(sketch, "E107.6.31.0", {"start": v(0.91, -13.48) * mm, "end": v(1.9, -13.37) * mm, "construction": true});
            skLineSegment(sketch, "E107.9.31.0", {"start": v(1.28, -12.18) * mm, "end": v(1.73, -12.14) * mm, "construction": true});
            skLineSegment(sketch, "E107.12.31.0", {"start": v(1.28, -12.18) * mm, "end": v(0.83, -12.23) * mm, "construction": true});
            skLineSegment(sketch, "E107.2.32.0", {"start": v(2.32, -13.3) * mm, "end": v(2.1, -12.07) * mm});
            skLineSegment(sketch, "E107.3.32.0", {"start": v(3.3, -13.1) * mm, "end": v(2.99, -11.88) * mm});
            skLineSegment(sketch, "E107.6.32.0", {"start": v(2.32, -13.3) * mm, "end": v(3.3, -13.1) * mm});
            skLineSegment(sketch, "E107.9.32.0", {"start": v(2.55, -11.98) * mm, "end": v(3, -11.89) * mm});
            skLineSegment(sketch, "E107.12.32.0", {"start": v(2.55, -11.98) * mm, "end": v(2.1, -12.08) * mm});
            skLineSegment(sketch, "E107.2.33.0", {"start": v(3.7, -13) * mm, "end": v(3.35, -11.78) * mm});
            skLineSegment(sketch, "E107.3.33.0", {"start": v(4.65, -12.68) * mm, "end": v(4.21, -11.5) * mm});
            skLineSegment(sketch, "E107.6.33.0", {"start": v(3.7, -13) * mm, "end": v(4.65, -12.68) * mm});
            skLineSegment(sketch, "E107.9.33.0", {"start": v(3.79, -11.65) * mm, "end": v(4.22, -11.51) * mm});
            skLineSegment(sketch, "E107.12.33.0", {"start": v(3.79, -11.65) * mm, "end": v(3.35, -11.8) * mm});
            skLineSegment(sketch, "E107.2.34.0", {"start": v(5.03, -12.54) * mm, "end": v(4.56, -11.37) * mm});
            skLineSegment(sketch, "E107.3.34.0", {"start": v(5.95, -12.13) * mm, "end": v(5.4, -11) * mm});
            skLineSegment(sketch, "E107.6.34.0", {"start": v(5.03, -12.54) * mm, "end": v(5.95, -12.13) * mm});
            skLineSegment(sketch, "E107.9.34.0", {"start": v(4.98, -11.2) * mm, "end": v(5.4, -11) * mm});
            skLineSegment(sketch, "E107.12.34.0", {"start": v(4.98, -11.2) * mm, "end": v(4.57, -11.38) * mm});
            skLineSegment(sketch, "E107.2.35.0", {"start": v(6.32, -11.94) * mm, "end": v(5.73, -10.83) * mm});
            skLineSegment(sketch, "E107.3.35.0", {"start": v(7.18, -11.44) * mm, "end": v(6.51, -10.37) * mm});
            skLineSegment(sketch, "E107.6.35.0", {"start": v(6.32, -11.94) * mm, "end": v(7.18, -11.44) * mm});
            skLineSegment(sketch, "E107.9.35.0", {"start": v(6.12, -10.6) * mm, "end": v(6.52, -10.38) * mm});
            skLineSegment(sketch, "E107.12.35.0", {"start": v(6.12, -10.6) * mm, "end": v(5.73, -10.84) * mm});
            skLineSegment(sketch, "E107.2.36.0", {"start": v(7.53, -11.22) * mm, "end": v(6.83, -10.17) * mm});
            skLineSegment(sketch, "E107.3.36.0", {"start": v(8.34, -10.63) * mm, "end": v(7.56, -9.64) * mm});
            skLineSegment(sketch, "E107.6.36.0", {"start": v(7.53, -11.22) * mm, "end": v(8.34, -10.63) * mm});
            skLineSegment(sketch, "E107.9.36.0", {"start": v(7.2, -9.91) * mm, "end": v(7.57, -9.64) * mm});
            skLineSegment(sketch, "E107.12.36.0", {"start": v(7.2, -9.91) * mm, "end": v(6.83, -10.18) * mm});
            skLineSegment(sketch, "E107.2.37.0", {"start": v(8.66, -10.37) * mm, "end": v(7.85, -9.4) * mm});
            skLineSegment(sketch, "E107.3.37.0", {"start": v(9.4, -9.7) * mm, "end": v(8.53, -8.8) * mm});
            skLineSegment(sketch, "E107.6.37.0", {"start": v(8.66, -10.37) * mm, "end": v(9.4, -9.7) * mm});
            skLineSegment(sketch, "E107.9.37.0", {"start": v(8.2, -9.1) * mm, "end": v(8.53, -8.8) * mm});
            skLineSegment(sketch, "E107.12.37.0", {"start": v(8.2, -9.1) * mm, "end": v(7.86, -9.4) * mm});
            skLineSegment(sketch, "E107.2.38.0", {"start": v(9.7, -9.4) * mm, "end": v(8.8, -8.53) * mm});
            skLineSegment(sketch, "E107.3.38.0", {"start": v(10.37, -8.66) * mm, "end": v(9.4, -7.85) * mm});
            skLineSegment(sketch, "E107.6.38.0", {"start": v(9.7, -9.4) * mm, "end": v(10.37, -8.66) * mm});
            skLineSegment(sketch, "E107.9.38.0", {"start": v(9.1, -8.2) * mm, "end": v(9.4, -7.86) * mm});
            skLineSegment(sketch, "E107.12.38.0", {"start": v(9.1, -8.2) * mm, "end": v(8.8, -8.53) * mm});
            skLineSegment(sketch, "E107.2.39.0", {"start": v(10.63, -8.34) * mm, "end": v(9.64, -7.56) * mm});
            skLineSegment(sketch, "E107.3.39.0", {"start": v(11.22, -7.53) * mm, "end": v(10.17, -6.83) * mm});
            skLineSegment(sketch, "E107.6.39.0", {"start": v(10.63, -8.34) * mm, "end": v(11.22, -7.53) * mm});
            skLineSegment(sketch, "E107.9.39.0", {"start": v(9.91, -7.2) * mm, "end": v(10.18, -6.83) * mm});
            skLineSegment(sketch, "E107.12.39.0", {"start": v(9.91, -7.2) * mm, "end": v(9.64, -7.57) * mm});
            skLineSegment(sketch, "E107.2.40.0", {"start": v(11.44, -7.18) * mm, "end": v(10.37, -6.51) * mm});
            skLineSegment(sketch, "E107.3.40.0", {"start": v(11.94, -6.32) * mm, "end": v(10.83, -5.73) * mm});
            skLineSegment(sketch, "E107.6.40.0", {"start": v(11.44, -7.18) * mm, "end": v(11.94, -6.32) * mm});
            skLineSegment(sketch, "E107.9.40.0", {"start": v(10.6, -6.13) * mm, "end": v(10.84, -5.73) * mm});
            skLineSegment(sketch, "E107.12.40.0", {"start": v(10.6, -6.13) * mm, "end": v(10.38, -6.52) * mm});
            skLineSegment(sketch, "E107.2.41.0", {"start": v(12.13, -5.95) * mm, "end": v(11, -5.4) * mm});
            skLineSegment(sketch, "E107.3.41.0", {"start": v(12.54, -5.03) * mm, "end": v(11.37, -4.56) * mm});
            skLineSegment(sketch, "E107.6.41.0", {"start": v(12.13, -5.95) * mm, "end": v(12.54, -5.03) * mm});
            skLineSegment(sketch, "E107.9.41.0", {"start": v(11.2, -4.98) * mm, "end": v(11.38, -4.57) * mm});
            skLineSegment(sketch, "E107.12.41.0", {"start": v(11.2, -4.98) * mm, "end": v(11, -5.4) * mm});
            skLineSegment(sketch, "E107.2.42.0", {"start": v(12.68, -4.65) * mm, "end": v(11.5, -4.21) * mm});
            skLineSegment(sketch, "E107.3.42.0", {"start": v(13, -3.7) * mm, "end": v(11.78, -3.35) * mm});
            skLineSegment(sketch, "E107.6.42.0", {"start": v(12.68, -4.65) * mm, "end": v(13, -3.7) * mm});
            skLineSegment(sketch, "E107.9.42.0", {"start": v(11.65, -3.79) * mm, "end": v(11.8, -3.35) * mm});
            skLineSegment(sketch, "E107.12.42.0", {"start": v(11.65, -3.79) * mm, "end": v(11.51, -4.22) * mm});
            skLineSegment(sketch, "E107.2.43.0", {"start": v(13.1, -3.3) * mm, "end": v(11.88, -2.99) * mm});
            skLineSegment(sketch, "E107.3.43.0", {"start": v(13.3, -2.32) * mm, "end": v(12.07, -2.1) * mm});
            skLineSegment(sketch, "E107.6.43.0", {"start": v(13.1, -3.3) * mm, "end": v(13.3, -2.32) * mm});
            skLineSegment(sketch, "E107.9.43.0", {"start": v(11.98, -2.55) * mm, "end": v(12.08, -2.1) * mm});
            skLineSegment(sketch, "E107.12.43.0", {"start": v(11.98, -2.55) * mm, "end": v(11.89, -3) * mm});
            skLineSegment(sketch, "E107.2.44.0", {"start": v(13.37, -1.9) * mm, "end": v(12.13, -1.73) * mm, "construction": true});
            skLineSegment(sketch, "E107.3.44.0", {"start": v(13.48, -0.91) * mm, "end": v(12.22, -0.83) * mm, "construction": true});
            skLineSegment(sketch, "E107.6.44.0", {"start": v(13.37, -1.9) * mm, "end": v(13.48, -0.91) * mm, "construction": true});
            skLineSegment(sketch, "E107.9.44.0", {"start": v(12.18, -1.28) * mm, "end": v(12.23, -0.83) * mm, "construction": true});
            skLineSegment(sketch, "E107.12.44.0", {"start": v(12.18, -1.28) * mm, "end": v(12.14, -1.73) * mm, "construction": true});
            skLineSegment(sketch, "E107.2.45.0", {"start": v(13.5, -0.5) * mm, "end": v(12.24, -0.45) * mm, "construction": true});
            skLineSegment(sketch, "E107.3.45.0", {"start": v(13.5, 0.5) * mm, "end": v(12.24, 0.45) * mm, "construction": true});
            skLineSegment(sketch, "E107.6.45.0", {"start": v(13.5, -0.5) * mm, "end": v(13.5, 0.5) * mm, "construction": true});
            skLineSegment(sketch, "E107.9.45.0", {"start": v(12.25, 0) * mm, "end": v(12.25, 0.45) * mm, "construction": true});
            skLineSegment(sketch, "E107.12.45.0", {"start": v(12.25, 0) * mm, "end": v(12.25, -0.45) * mm, "construction": true});
            skLineSegment(sketch, "E107.2.46.0", {"start": v(13.48, 0.91) * mm, "end": v(12.22, 0.83) * mm, "construction": true});
            skLineSegment(sketch, "E107.3.46.0", {"start": v(13.37, 1.9) * mm, "end": v(12.13, 1.73) * mm, "construction": true});
            skLineSegment(sketch, "E107.6.46.0", {"start": v(13.48, 0.91) * mm, "end": v(13.37, 1.9) * mm, "construction": true});
            skLineSegment(sketch, "E107.9.46.0", {"start": v(12.18, 1.28) * mm, "end": v(12.14, 1.73) * mm, "construction": true});
            skLineSegment(sketch, "E107.12.46.0", {"start": v(12.18, 1.28) * mm, "end": v(12.23, 0.83) * mm, "construction": true});
            skLineSegment(sketch, "E107.2.47.0", {"start": v(13.3, 2.32) * mm, "end": v(12.07, 2.1) * mm});
            skLineSegment(sketch, "E107.3.47.0", {"start": v(13.1, 3.3) * mm, "end": v(11.88, 2.99) * mm});
            skLineSegment(sketch, "E107.6.47.0", {"start": v(13.3, 2.32) * mm, "end": v(13.1, 3.3) * mm});
            skLineSegment(sketch, "E107.9.47.0", {"start": v(11.98, 2.55) * mm, "end": v(11.89, 3) * mm});
            skLineSegment(sketch, "E107.12.47.0", {"start": v(11.98, 2.55) * mm, "end": v(12.08, 2.1) * mm});
            skLineSegment(sketch, "E107.2.48.0", {"start": v(13, 3.7) * mm, "end": v(11.78, 3.35) * mm});
            skLineSegment(sketch, "E107.3.48.0", {"start": v(12.68, 4.65) * mm, "end": v(11.5, 4.21) * mm});
            skLineSegment(sketch, "E107.6.48.0", {"start": v(13, 3.7) * mm, "end": v(12.68, 4.65) * mm});
            skLineSegment(sketch, "E107.9.48.0", {"start": v(11.65, 3.79) * mm, "end": v(11.51, 4.22) * mm});
            skLineSegment(sketch, "E107.12.48.0", {"start": v(11.65, 3.79) * mm, "end": v(11.8, 3.35) * mm});
            skLineSegment(sketch, "E107.2.49.0", {"start": v(12.54, 5.03) * mm, "end": v(11.37, 4.56) * mm});
            skLineSegment(sketch, "E107.3.49.0", {"start": v(12.13, 5.95) * mm, "end": v(11, 5.4) * mm});
            skLineSegment(sketch, "E107.6.49.0", {"start": v(12.54, 5.03) * mm, "end": v(12.13, 5.95) * mm});
            skLineSegment(sketch, "E107.9.49.0", {"start": v(11.2, 4.98) * mm, "end": v(11, 5.4) * mm});
            skLineSegment(sketch, "E107.12.49.0", {"start": v(11.2, 4.98) * mm, "end": v(11.38, 4.57) * mm});
            skLineSegment(sketch, "E107.2.50.0", {"start": v(11.94, 6.32) * mm, "end": v(10.83, 5.73) * mm});
            skLineSegment(sketch, "E107.3.50.0", {"start": v(11.44, 7.18) * mm, "end": v(10.37, 6.51) * mm});
            skLineSegment(sketch, "E107.6.50.0", {"start": v(11.94, 6.32) * mm, "end": v(11.44, 7.18) * mm});
            skLineSegment(sketch, "E107.9.50.0", {"start": v(10.6, 6.13) * mm, "end": v(10.38, 6.52) * mm});
            skLineSegment(sketch, "E107.12.50.0", {"start": v(10.6, 6.13) * mm, "end": v(10.84, 5.73) * mm});
            skLineSegment(sketch, "E107.2.51.0", {"start": v(11.22, 7.53) * mm, "end": v(10.17, 6.83) * mm});
            skLineSegment(sketch, "E107.3.51.0", {"start": v(10.63, 8.34) * mm, "end": v(9.64, 7.56) * mm});
            skLineSegment(sketch, "E107.6.51.0", {"start": v(11.22, 7.53) * mm, "end": v(10.63, 8.34) * mm});
            skLineSegment(sketch, "E107.9.51.0", {"start": v(9.91, 7.2) * mm, "end": v(9.64, 7.57) * mm});
            skLineSegment(sketch, "E107.12.51.0", {"start": v(9.91, 7.2) * mm, "end": v(10.18, 6.83) * mm});
            skLineSegment(sketch, "E107.2.52.0", {"start": v(10.37, 8.66) * mm, "end": v(9.4, 7.85) * mm});
            skLineSegment(sketch, "E107.3.52.0", {"start": v(9.7, 9.4) * mm, "end": v(8.8, 8.53) * mm});
            skLineSegment(sketch, "E107.6.52.0", {"start": v(10.37, 8.66) * mm, "end": v(9.7, 9.4) * mm});
            skLineSegment(sketch, "E107.9.52.0", {"start": v(9.1, 8.2) * mm, "end": v(8.8, 8.53) * mm});
            skLineSegment(sketch, "E107.12.52.0", {"start": v(9.1, 8.2) * mm, "end": v(9.4, 7.86) * mm});
            skLineSegment(sketch, "E107.2.53.0", {"start": v(9.4, 9.7) * mm, "end": v(8.53, 8.8) * mm});
            skLineSegment(sketch, "E107.3.53.0", {"start": v(8.66, 10.37) * mm, "end": v(7.85, 9.4) * mm});
            skLineSegment(sketch, "E107.6.53.0", {"start": v(9.4, 9.7) * mm, "end": v(8.66, 10.37) * mm});
            skLineSegment(sketch, "E107.9.53.0", {"start": v(8.2, 9.1) * mm, "end": v(7.86, 9.4) * mm});
            skLineSegment(sketch, "E107.12.53.0", {"start": v(8.2, 9.1) * mm, "end": v(8.53, 8.8) * mm});
            skLineSegment(sketch, "E107.2.54.0", {"start": v(8.34, 10.63) * mm, "end": v(7.56, 9.64) * mm});
            skLineSegment(sketch, "E107.3.54.0", {"start": v(7.53, 11.22) * mm, "end": v(6.83, 10.17) * mm});
            skLineSegment(sketch, "E107.6.54.0", {"start": v(8.34, 10.63) * mm, "end": v(7.53, 11.22) * mm});
            skLineSegment(sketch, "E107.9.54.0", {"start": v(7.2, 9.91) * mm, "end": v(6.83, 10.18) * mm});
            skLineSegment(sketch, "E107.12.54.0", {"start": v(7.2, 9.91) * mm, "end": v(7.57, 9.64) * mm});
            skLineSegment(sketch, "E107.2.55.0", {"start": v(7.18, 11.44) * mm, "end": v(6.51, 10.37) * mm});
            skLineSegment(sketch, "E107.3.55.0", {"start": v(6.32, 11.94) * mm, "end": v(5.73, 10.83) * mm});
            skLineSegment(sketch, "E107.6.55.0", {"start": v(7.18, 11.44) * mm, "end": v(6.32, 11.94) * mm});
            skLineSegment(sketch, "E107.9.55.0", {"start": v(6.12, 10.6) * mm, "end": v(5.73, 10.84) * mm});
            skLineSegment(sketch, "E107.12.55.0", {"start": v(6.12, 10.6) * mm, "end": v(6.52, 10.38) * mm});
            skLineSegment(sketch, "E107.2.56.0", {"start": v(5.95, 12.13) * mm, "end": v(5.4, 11) * mm});
            skLineSegment(sketch, "E107.3.56.0", {"start": v(5.03, 12.54) * mm, "end": v(4.56, 11.37) * mm});
            skLineSegment(sketch, "E107.6.56.0", {"start": v(5.95, 12.13) * mm, "end": v(5.03, 12.54) * mm});
            skLineSegment(sketch, "E107.9.56.0", {"start": v(4.98, 11.2) * mm, "end": v(4.57, 11.38) * mm});
            skLineSegment(sketch, "E107.12.56.0", {"start": v(4.98, 11.2) * mm, "end": v(5.4, 11) * mm});
            skLineSegment(sketch, "E107.2.57.0", {"start": v(4.65, 12.68) * mm, "end": v(4.21, 11.5) * mm});
            skLineSegment(sketch, "E107.3.57.0", {"start": v(3.7, 13) * mm, "end": v(3.35, 11.78) * mm});
            skLineSegment(sketch, "E107.6.57.0", {"start": v(4.65, 12.68) * mm, "end": v(3.7, 13) * mm});
            skLineSegment(sketch, "E107.9.57.0", {"start": v(3.79, 11.65) * mm, "end": v(3.35, 11.8) * mm});
            skLineSegment(sketch, "E107.12.57.0", {"start": v(3.79, 11.65) * mm, "end": v(4.22, 11.51) * mm});
            skLineSegment(sketch, "E107.2.58.0", {"start": v(3.3, 13.1) * mm, "end": v(2.99, 11.88) * mm});
            skLineSegment(sketch, "E107.3.58.0", {"start": v(2.32, 13.3) * mm, "end": v(2.1, 12.07) * mm});
            skLineSegment(sketch, "E107.6.58.0", {"start": v(3.3, 13.1) * mm, "end": v(2.32, 13.3) * mm});
            skLineSegment(sketch, "E107.9.58.0", {"start": v(2.55, 11.98) * mm, "end": v(2.1, 12.08) * mm});
            skLineSegment(sketch, "E107.12.58.0", {"start": v(2.55, 11.98) * mm, "end": v(3, 11.89) * mm});
            skLineSegment(sketch, "E107.2.59.0", {"start": v(1.9, 13.37) * mm, "end": v(1.73, 12.13) * mm, "construction": true});
            skLineSegment(sketch, "E107.3.59.0", {"start": v(0.91, 13.48) * mm, "end": v(0.83, 12.22) * mm, "construction": true});
            skLineSegment(sketch, "E107.6.59.0", {"start": v(1.9, 13.37) * mm, "end": v(0.91, 13.48) * mm, "construction": true});
            skLineSegment(sketch, "E107.9.59.0", {"start": v(1.28, 12.18) * mm, "end": v(0.83, 12.23) * mm, "construction": true});
            skLineSegment(sketch, "E107.12.59.0", {"start": v(1.28, 12.18) * mm, "end": v(1.73, 12.14) * mm, "construction": true});
            skSolve(sketch);
        }
        {
            var Q0;
            Q0=qSketchRegion(id+"F3",true);
            extrude(context, id + "F6", {"entities" : qUnion([Q0]), "depth" : 0.2 * mm});
        }
    });
